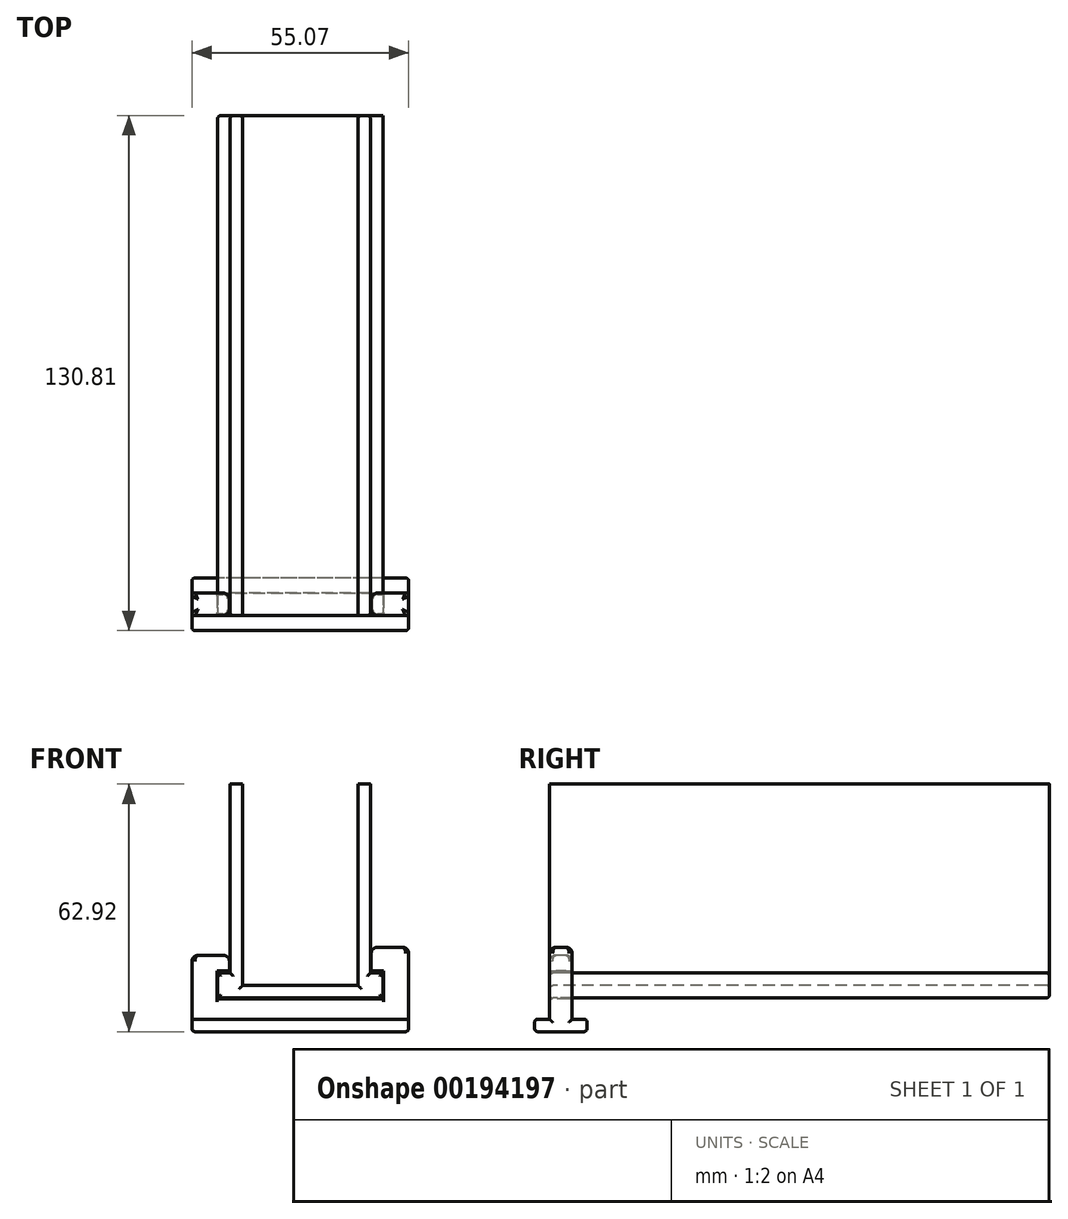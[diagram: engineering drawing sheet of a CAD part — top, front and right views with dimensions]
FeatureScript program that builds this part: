
annotation { "Feature Type Name" : "Feature", "Feature Type Description" : "" }
export const myFeature = defineFeature(function(context is Context, id is Id, definition is map)
    precondition{}
    {
        {
            var Q0;
            Q0=qCreatedBy(makeId("Front.planeOp"),FACE);
            var sketch = newSketch(context, id + "F0", { "sketchPlane" : qUnion([Q0])});
            skLineSegment(sketch, "E0", {"start": v(0, 8.52) * mm, "end": v(0, 0) * mm, "construction": true});
            skLineSegment(sketch, "E1.0", {"start": v(13.51, -0.38) * mm, "end": v(13.51, 50.8) * mm});
            skLineSegment(sketch, "E1.5", {"start": v(-15.8, 50.8) * mm, "end": v(-15.8, -0.38) * mm});
            skLineSegment(sketch, "E1.8", {"start": v(13.51, -0.38) * mm, "end": v(-15.8, -0.38) * mm});
            skLineSegment(sketch, "E2", {"start": v(-15.8, 50.8) * mm, "end": v(-18.97, 50.8) * mm});
            skLineSegment(sketch, "E3", {"start": v(-18.97, 50.8) * mm, "end": v(-18.97, 2.8) * mm});
            skLineSegment(sketch, "E4", {"start": v(-18.97, 2.8) * mm, "end": v(-22.15, 2.8) * mm});
            skLineSegment(sketch, "E5", {"start": v(-22.15, 2.8) * mm, "end": v(-22.15, -3.56) * mm});
            skLineSegment(sketch, "E6", {"start": v(-22.15, -3.56) * mm, "end": v(19.86, -3.56) * mm});
            skCircle(sketch, "E7", {"center": v(0, 5.02) * mm, "radius": 1.7 * mm, "construction": true});
            skLineSegment(sketch, "E8", {"start": v(13.51, 50.8) * mm, "end": v(16.69, 50.8) * mm});
            skLineSegment(sketch, "E9", {"start": v(16.69, 50.8) * mm, "end": v(16.69, 2.8) * mm});
            skLineSegment(sketch, "E10", {"start": v(16.69, 2.8) * mm, "end": v(19.86, 2.8) * mm});
            skLineSegment(sketch, "E11", {"start": v(19.86, 2.8) * mm, "end": v(19.86, -3.56) * mm});
            skLineSegment(sketch, "E12.0", {"start": v(16.87, 50.8) * mm, "end": v(16.87, 2.97) * mm});
            skLineSegment(sketch, "E12.1", {"start": v(16.87, 2.97) * mm, "end": v(20.04, 2.97) * mm});
            skLineSegment(sketch, "E12.2", {"start": v(20.04, 2.97) * mm, "end": v(20.04, -3.73) * mm});
            skLineSegment(sketch, "E12.3", {"start": v(-19.15, 50.8) * mm, "end": v(-19.15, 2.97) * mm});
            skLineSegment(sketch, "E12.4", {"start": v(-19.15, 2.97) * mm, "end": v(-22.33, 2.97) * mm});
            skLineSegment(sketch, "E12.5", {"start": v(-22.33, 2.97) * mm, "end": v(-22.33, -3.73) * mm});
            skLineSegment(sketch, "E12.6", {"start": v(-22.33, -3.73) * mm, "end": v(20.04, -3.73) * mm});
            skLineSegment(sketch, "E13.1", {"start": v(16.87, 9.32) * mm, "end": v(26.4, 9.32) * mm});
            skLineSegment(sketch, "E13.2", {"start": v(26.4, 9.32) * mm, "end": v(26.4, -12.12) * mm});
            skLineSegment(sketch, "E13.4", {"start": v(-19.15, 7.29) * mm, "end": v(-28.68, 7.29) * mm});
            skLineSegment(sketch, "E13.5", {"start": v(-28.68, 7.29) * mm, "end": v(-28.68, -12.12) * mm});
            skLineSegment(sketch, "E13.6", {"start": v(-28.68, -12.12) * mm, "end": v(26.4, -12.12) * mm});
            skSolve(sketch);
        }
        {
            var Q0;
            {var subQ1=sQuery(id+"F0.wireOp",EDGE,"E12.1");Q0=makeQuery(id+"F0.imprint","IMPRINT",FACE,{"disambiguationData":[TD([[makeQuery(id+"F0.imprint","IMPRINT",EDGE,{"derivedFrom":subQ1}),1.0]])]});}
            extrude(context, id + "F1", {"entities" : qUnion([Q0]), "oppositeDirection" : true, "depth" : 5.7 * mm});
        }
        {
            var Q0;
            Q0=makeQuery(id+"F1.opExtrude","CAP_EDGE",EDGE,{"disambiguationData":[OSD([sQuery(id+"F0.wireOp",EDGE,"E12.0")])],"isStart":true});
            var Q1;
            Q1=makeQuery(id+"F1.opExtrude","CAP_EDGE",EDGE,{"disambiguationData":[OSD([sQuery(id+"F0.wireOp",EDGE,"E12.0")])],"isStart":false});
            var Q2;
            Q2=makeQuery(id+"F1.opExtrude","CAP_EDGE",EDGE,{"disambiguationData":[OSD([sQuery(id+"F0.wireOp",EDGE,"E12.3")])],"isStart":true});
            var Q3;
            Q3=makeQuery(id+"F1.opExtrude","CAP_EDGE",EDGE,{"disambiguationData":[OSD([sQuery(id+"F0.wireOp",EDGE,"E13.4")])],"isStart":false});
            var Q4;
            Q4=makeQuery(id+"F1.opExtrude","CAP_EDGE",EDGE,{"disambiguationData":[OSD([sQuery(id+"F0.wireOp",EDGE,"E13.1")])],"isStart":false});
            var Q5;
            Q5=makeQuery(id+"F1.opExtrude","SWEPT_EDGE",EDGE,{"disambiguationData":[OSD([sQuery(id+"F0.wireOp",EDGE,"E12.3"),sQuery(id+"F0.wireOp",EDGE,"E13.4")])]});
            var Q6;
            Q6=makeQuery(id+"F1.opExtrude","SWEPT_EDGE",EDGE,{"disambiguationData":[OSD([sQuery(id+"F0.wireOp",EDGE,"E12.0"),sQuery(id+"F0.wireOp",EDGE,"E13.1")])]});
            var Q7;
            Q7=makeQuery(id+"F1.opExtrude","SWEPT_EDGE",EDGE,{"disambiguationData":[OSD([sQuery(id+"F0.wireOp",EDGE,"E13.4"),sQuery(id+"F0.wireOp",EDGE,"E13.5")])]});
            var Q8;
            Q8=makeQuery(id+"F1.opExtrude","SWEPT_EDGE",EDGE,{"disambiguationData":[OSD([sQuery(id+"F0.wireOp",EDGE,"E13.1"),sQuery(id+"F0.wireOp",EDGE,"E13.2")])]});
            var Q9;
            Q9=makeQuery(id+"F1.opExtrude","CAP_EDGE",EDGE,{"disambiguationData":[OSD([sQuery(id+"F0.wireOp",EDGE,"E13.1")])],"isStart":true});
            var Q10;
            Q10=makeQuery(id+"F1.opExtrude","CAP_EDGE",EDGE,{"disambiguationData":[OSD([sQuery(id+"F0.wireOp",EDGE,"E13.4")])],"isStart":true});
            var Q11;
            Q11=makeQuery(id+"F1.opExtrude","CAP_EDGE",EDGE,{"disambiguationData":[OSD([sQuery(id+"F0.wireOp",EDGE,"E12.3")])],"isStart":false});
            fillet(context, id + "F2", {"entities" : qUnion([Q0, Q1, Q2, Q3, Q4, Q5, Q6, Q7, Q8, Q9, Q10, Q11]), "radius" : 1.57 * mm, "tangentPropagation" : true, "allowEdgeOverflow" : false});
        }
        {
            var Q0;
            Q0=makeQuery(id+"F1.opExtrude","SWEPT_EDGE",EDGE,{"disambiguationData":[OSD([sQuery(id+"F0.wireOp",EDGE,"E12.0"),sQuery(id+"F0.wireOp",EDGE,"E12.1")])]});
            var Q1;
            Q1=makeQuery(id+"F1.opExtrude","SWEPT_EDGE",EDGE,{"disambiguationData":[OSD([sQuery(id+"F0.wireOp",EDGE,"E12.3"),sQuery(id+"F0.wireOp",EDGE,"E12.4")])]});
            chamfer(context, id + "F3", {"entities" : qUnion([Q0, Q1]), "width" : 0.38 * mm, "tangentPropagation" : true});
        }
        {
            var Q0;
            Q0=qCreatedBy(makeId("Right.planeOp"),FACE);
            var sketch = newSketch(context, id + "F4", { "sketchPlane" : qUnion([Q0])});
            skLineSegment(sketch, "E14.0", {"start": v(5.72, -12.12) * mm, "end": v(0, -12.12) * mm});
            skLineSegment(sketch, "E15.0", {"start": v(0, 7.75) * mm, "end": v(0, -12.12) * mm});
            skLineSegment(sketch, "E16.0", {"start": v(5.72, 7.75) * mm, "end": v(5.72, -12.12) * mm});
            skLineSegment(sketch, "E17", {"start": v(0, -8.94) * mm, "end": v(-3.81, -8.94) * mm});
            skLineSegment(sketch, "E18", {"start": v(-3.81, -8.94) * mm, "end": v(-3.81, -12.12) * mm});
            skLineSegment(sketch, "E19", {"start": v(-3.81, -12.12) * mm, "end": v(0, -12.12) * mm});
            skLineSegment(sketch, "E20", {"start": v(5.72, -8.94) * mm, "end": v(9.53, -8.94) * mm});
            skLineSegment(sketch, "E21", {"start": v(9.53, -8.94) * mm, "end": v(9.53, -12.12) * mm});
            skLineSegment(sketch, "E22", {"start": v(9.53, -12.12) * mm, "end": v(5.72, -12.12) * mm});
            skSolve(sketch);
        }
        {
            var Q0;
            {var subQ2=sQuery(id+"F4.wireOp",EDGE,"E17");Q0=makeQuery(id+"F4.imprint","IMPRINT",FACE,{"disambiguationData":[TD([[makeQuery(id+"F4.imprint","IMPRINT",EDGE,{"derivedFrom":subQ2}),1.0]])]});}
            var Q1;
            {var subQ2=sQuery(id+"F4.wireOp",EDGE,"E20");Q1=makeQuery(id+"F4.imprint","IMPRINT",FACE,{"disambiguationData":[TD([[makeQuery(id+"F4.imprint","IMPRINT",EDGE,{"derivedFrom":subQ2}),-1.0]])]});}
            extrude(context, id + "F5", {"entities" : qUnion([Q0, Q1]), "operationType" : NewBodyOperationType.ADD, "depth" : 26.4 * mm, "hasSecondDirection" : true, "secondDirectionOppositeDirection" : true, "secondDirectionDepth" : 28.68 * mm});
        }
        {
            var Q0;
            Q0=makeQuery(id+"F5.opExtrude","SWEPT_EDGE",EDGE,{"disambiguationData":[OSD([sQuery(id+"F4.wireOp",EDGE,"E17"),sQuery(id+"F4.wireOp",EDGE,"E18")])]});
            var Q1;
            Q1=makeQuery(id+"F5.opExtrude","SWEPT_EDGE",EDGE,{"disambiguationData":[OSD([sQuery(id+"F4.wireOp",EDGE,"E18"),sQuery(id+"F4.wireOp",EDGE,"E19")])]});
            var Q2;
            Q2=makeQuery(id+"F5.opExtrude","SWEPT_EDGE",EDGE,{"disambiguationData":[OSD([sQuery(id+"F4.wireOp",EDGE,"E20"),sQuery(id+"F4.wireOp",EDGE,"E21")])]});
            var Q3;
            Q3=makeQuery(id+"F5.opExtrude","SWEPT_EDGE",EDGE,{"disambiguationData":[OSD([sQuery(id+"F4.wireOp",EDGE,"E21"),sQuery(id+"F4.wireOp",EDGE,"E22")])]});
            var Q4;
            Q4=makeQuery(id+"F1.opExtrude","CAP_EDGE",EDGE,{"disambiguationData":[OSD([sQuery(id+"F0.wireOp",EDGE,"E13.2")])],"isStart":false});
            var Q5;
            Q5=makeQuery(id+"F1.opExtrude","CAP_EDGE",EDGE,{"disambiguationData":[OSD([sQuery(id+"F0.wireOp",EDGE,"E13.2")])],"isStart":true});
            var Q6;
            Q6=makeQuery(id+"F1.opExtrude","CAP_EDGE",EDGE,{"disambiguationData":[OSD([sQuery(id+"F0.wireOp",EDGE,"E13.5")])],"isStart":true});
            var Q7;
            Q7=makeQuery(id+"F1.opExtrude","CAP_EDGE",EDGE,{"disambiguationData":[OSD([sQuery(id+"F0.wireOp",EDGE,"E13.5")])],"isStart":false});
            var Q8;
            Q8=makeQuery(id+"F5.opExtrude","CAP_EDGE",EDGE,{"disambiguationData":[OSD([sQuery(id+"F4.wireOp",EDGE,"E20")])],"isStart":true});
            var Q9;
            Q9=makeQuery(id+"F5.opExtrude","CAP_EDGE",EDGE,{"disambiguationData":[OSD([sQuery(id+"F4.wireOp",EDGE,"E17")])],"isStart":true});
            var Q10;
            Q10=makeQuery(id+"F5.opExtrude","CAP_EDGE",EDGE,{"disambiguationData":[OSD([sQuery(id+"F4.wireOp",EDGE,"E17")])],"isStart":false});
            var Q11;
            Q11=makeQuery(id+"F5.opExtrude","CAP_EDGE",EDGE,{"disambiguationData":[OSD([sQuery(id+"F4.wireOp",EDGE,"E20")])],"isStart":false});
            var Q12;
            Q12=makeQuery(id+"F1.opExtrude","CAP_EDGE",EDGE,{"disambiguationData":[OSD([sQuery(id+"F0.wireOp",EDGE,"E12.6")])],"isStart":true});
            var Q13;
            Q13=makeQuery(id+"F1.opExtrude","CAP_EDGE",EDGE,{"disambiguationData":[OSD([sQuery(id+"F0.wireOp",EDGE,"E12.6")])],"isStart":false});
            var Q14;
            Q14=makeQuery(id+"F5.opExtrude","CAP_EDGE",EDGE,{"disambiguationData":[OSD([sQuery(id+"F4.wireOp",EDGE,"E21")])],"isStart":true});
            var Q15;
            Q15=makeQuery(id+"F5.opExtrude","CAP_EDGE",EDGE,{"disambiguationData":[OSD([sQuery(id+"F4.wireOp",EDGE,"E18")])],"isStart":true});
            var Q16;
            Q16=makeQuery(id+"F5.opExtrude","CAP_EDGE",EDGE,{"disambiguationData":[OSD([sQuery(id+"F4.wireOp",EDGE,"E18")])],"isStart":false});
            var Q17;
            Q17=makeQuery(id+"F5.opExtrude","CAP_EDGE",EDGE,{"disambiguationData":[OSD([sQuery(id+"F4.wireOp",EDGE,"E21")])],"isStart":false});
            var Q18;
            Q18=makeQuery(id+"F5.boolean.opBoolean","MERGE",EDGE,{"derivedFrom":[makeQuery(id+"F1.opExtrude","SWEPT_EDGE",EDGE,{"disambiguationData":[OSD([sQuery(id+"F0.wireOp",EDGE,"E13.2"),sQuery(id+"F0.wireOp",EDGE,"E13.6")])]}),makeQuery(id+"F5.opExtrude","CAP_EDGE",EDGE,{"disambiguationData":[OSD([sQuery(id+"F4.wireOp",EDGE,"E19")])],"isStart":false}),makeQuery(id+"F5.opExtrude","CAP_EDGE",EDGE,{"disambiguationData":[OSD([sQuery(id+"F4.wireOp",EDGE,"E22")])],"isStart":false})]});
            var Q19;
            Q19=makeQuery(id+"F5.boolean.opBoolean","MERGE",EDGE,{"derivedFrom":[makeQuery(id+"F1.opExtrude","SWEPT_EDGE",EDGE,{"disambiguationData":[OSD([sQuery(id+"F0.wireOp",EDGE,"E13.5"),sQuery(id+"F0.wireOp",EDGE,"E13.6")])]}),makeQuery(id+"F5.opExtrude","CAP_EDGE",EDGE,{"disambiguationData":[OSD([sQuery(id+"F4.wireOp",EDGE,"E19")])],"isStart":true}),makeQuery(id+"F5.opExtrude","CAP_EDGE",EDGE,{"disambiguationData":[OSD([sQuery(id+"F4.wireOp",EDGE,"E22")])],"isStart":true})]});
            fillet(context, id + "F6", {"entities" : qUnion([Q0, Q1, Q2, Q3, Q4, Q5, Q6, Q7, Q8, Q9, Q10, Q11, Q12, Q13, Q14, Q15, Q16, Q17, Q18, Q19]), "radius" : 0.79 * mm, "tangentPropagation" : true, "allowEdgeOverflow" : false});
        }
        {
            var Q0;
            Q0=makeQuery(id+"F0.imprint","IMPRINT",FACE,{"disambiguationData":[TD([[makeQuery(id+"F0.imprint","IMPRINT",EDGE,{"derivedFrom":sQuery(id+"F0.wireOp",EDGE,"E1.0")}),-1.0]])]});
            extrude(context, id + "F7", {"entities" : qUnion([Q0]), "oppositeDirection" : true, "depth" : 127 * mm});
        }
        {
            var Q0;
            Q0=makeQuery(id+"F9.boolean.opBoolean","INTERSECT",EDGE,{"derivedFrom":[makeQuery(id+"F7.opExtrude","SWEPT_FACE",FACE,{"disambiguationData":[OSD([sQuery(id+"F0.wireOp",EDGE,"E3")])]}),makeQuery(id+"F9.opExtrude","SWEPT_FACE",FACE,{"disambiguationData":[OSD([sQuery(id+"FkgncSVRvIpgr8o_1.wireOp",EDGE,"zSHfNMzP-miez-my1W-6nEw-eT44UZ99gvPm")])]})]});
            var Q1;
            Q1=makeQuery(id+"F9.boolean.opBoolean","INTERSECT",EDGE,{"derivedFrom":[makeQuery(id+"F7.opExtrude","SWEPT_FACE",FACE,{"disambiguationData":[OSD([sQuery(id+"F0.wireOp",EDGE,"E1.5")])]}),makeQuery(id+"F9.opExtrude","SWEPT_FACE",FACE,{"disambiguationData":[OSD([sQuery(id+"FkgncSVRvIpgr8o_1.wireOp",EDGE,"zSHfNMzP-miez-my1W-6nEw-eT44UZ99gvPm")])]})]});
            var Q2;
            Q2=makeQuery(id+"F7.opExtrude","CAP_EDGE",EDGE,{"disambiguationData":[OSD([sQuery(id+"F0.wireOp",EDGE,"E1.5")])],"isStart":true});
            var Q3;
            Q3=makeQuery(id+"F7.opExtrude","CAP_EDGE",EDGE,{"disambiguationData":[OSD([sQuery(id+"F0.wireOp",EDGE,"E9")])],"isStart":true});
            var Q4;
            Q4=makeQuery(id+"F9.boolean.opBoolean","INTERSECT",EDGE,{"derivedFrom":[makeQuery(id+"F7.opExtrude","SWEPT_FACE",FACE,{"disambiguationData":[OSD([sQuery(id+"F0.wireOp",EDGE,"E9")])]}),makeQuery(id+"F9.opExtrude","SWEPT_FACE",FACE,{"disambiguationData":[OSD([sQuery(id+"FkgncSVRvIpgr8o_1.wireOp",EDGE,"zSHfNMzP-miez-my1W-6nEw-eT44UZ99gvPm")])]})]});
            var Q5;
            Q5=makeQuery(id+"F9.boolean.opBoolean","INTERSECT",EDGE,{"derivedFrom":[makeQuery(id+"F7.opExtrude","SWEPT_FACE",FACE,{"disambiguationData":[OSD([sQuery(id+"F0.wireOp",EDGE,"E1.0")])]}),makeQuery(id+"F9.opExtrude","SWEPT_FACE",FACE,{"disambiguationData":[OSD([sQuery(id+"FkgncSVRvIpgr8o_1.wireOp",EDGE,"zSHfNMzP-miez-my1W-6nEw-eT44UZ99gvPm")])]})]});
            var Q6;
            Q6=makeQuery(id+"F7.opExtrude","CAP_EDGE",EDGE,{"disambiguationData":[OSD([sQuery(id+"F0.wireOp",EDGE,"E1.8")])],"isStart":true});
            var Q7;
            Q7=makeQuery(id+"F7.opExtrude","CAP_EDGE",EDGE,{"disambiguationData":[OSD([sQuery(id+"F0.wireOp",EDGE,"E3")])],"isStart":true});
            var Q8;
            Q8=makeQuery(id+"F7.opExtrude","CAP_EDGE",EDGE,{"disambiguationData":[OSD([sQuery(id+"F0.wireOp",EDGE,"E1.0")])],"isStart":true});
            var Q9;
            Q9=makeQuery(id+"F7.opExtrude","CAP_EDGE",EDGE,{"disambiguationData":[OSD([sQuery(id+"F0.wireOp",EDGE,"E6")])],"isStart":true});
            var Q10;
            Q10=makeQuery(id+"F7.opExtrude","CAP_EDGE",EDGE,{"disambiguationData":[OSD([sQuery(id+"F0.wireOp",EDGE,"E10")])],"isStart":true});
            var Q11;
            Q11=makeQuery(id+"F7.opExtrude","CAP_EDGE",EDGE,{"disambiguationData":[OSD([sQuery(id+"F0.wireOp",EDGE,"E11")])],"isStart":true});
            var Q12;
            Q12=makeQuery(id+"F7.opExtrude","CAP_EDGE",EDGE,{"disambiguationData":[OSD([sQuery(id+"F0.wireOp",EDGE,"E4")])],"isStart":true});
            var Q13;
            Q13=makeQuery(id+"F7.opExtrude","CAP_EDGE",EDGE,{"disambiguationData":[OSD([sQuery(id+"F0.wireOp",EDGE,"E5")])],"isStart":true});
            var Q14;
            Q14=makeQuery(id+"F8.boolean.opBoolean","INTERSECT",EDGE,{"derivedFrom":[makeQuery(id+"F7.opExtrude","SWEPT_FACE",FACE,{"disambiguationData":[OSD([sQuery(id+"F0.wireOp",EDGE,"E1.5")])]}),makeQuery(id+"F8.opExtrude","SWEPT_FACE",FACE,{"disambiguationData":[OSD([sQuery(id+"Fb2vMvGs9BCBtCK_1.wireOp",EDGE,"JCwaT7HA-nb2K-ZSJl-F4ic-s2mm5Mdn0rMo")])]})]});
            var Q15;
            Q15=makeQuery(id+"F8.boolean.opBoolean","INTERSECT",EDGE,{"derivedFrom":[makeQuery(id+"F7.opExtrude","SWEPT_FACE",FACE,{"disambiguationData":[OSD([sQuery(id+"F0.wireOp",EDGE,"E1.5")])]}),makeQuery(id+"F8.opExtrude","SWEPT_FACE",FACE,{"disambiguationData":[OSD([sQuery(id+"Fb2vMvGs9BCBtCK_1.wireOp",EDGE,"NnNVMowN-uRfN-1ljK-sG6J-4kigYHrPbNCR")])]})]});
            var Q16;
            Q16=makeQuery(id+"F8.boolean.opBoolean","INTERSECT",EDGE,{"derivedFrom":[makeQuery(id+"F7.opExtrude","SWEPT_FACE",FACE,{"disambiguationData":[OSD([sQuery(id+"F0.wireOp",EDGE,"E1.0")])]}),makeQuery(id+"F8.opExtrude","SWEPT_FACE",FACE,{"disambiguationData":[OSD([sQuery(id+"Fb2vMvGs9BCBtCK_1.wireOp",EDGE,"JCwaT7HA-nb2K-ZSJl-F4ic-s2mm5Mdn0rMo")])]})]});
            var Q17;
            Q17=makeQuery(id+"F8.boolean.opBoolean","INTERSECT",EDGE,{"derivedFrom":[makeQuery(id+"F7.opExtrude","SWEPT_FACE",FACE,{"disambiguationData":[OSD([sQuery(id+"F0.wireOp",EDGE,"E1.0")])]}),makeQuery(id+"F8.opExtrude","SWEPT_FACE",FACE,{"disambiguationData":[OSD([sQuery(id+"Fb2vMvGs9BCBtCK_1.wireOp",EDGE,"NnNVMowN-uRfN-1ljK-sG6J-4kigYHrPbNCR")])]})]});
            var Q18;
            Q18=makeQuery(id+"F8.boolean.opBoolean","INTERSECT",EDGE,{"derivedFrom":[makeQuery(id+"F7.opExtrude","SWEPT_FACE",FACE,{"disambiguationData":[OSD([sQuery(id+"F0.wireOp",EDGE,"E1.0")])]}),makeQuery(id+"F8.opExtrude","SWEPT_FACE",FACE,{"disambiguationData":[OSD([sQuery(id+"Fb2vMvGs9BCBtCK_1.wireOp",EDGE,"cyouxJAX-TsAO-8wIh-7wvX-UbvCRropZ8Xa")])]})]});
            var Q19;
            Q19=makeQuery(id+"F8.boolean.opBoolean","INTERSECT",EDGE,{"derivedFrom":[makeQuery(id+"F7.opExtrude","SWEPT_FACE",FACE,{"disambiguationData":[OSD([sQuery(id+"F0.wireOp",EDGE,"E1.0")])]}),makeQuery(id+"F8.opExtrude","SWEPT_FACE",FACE,{"disambiguationData":[OSD([sQuery(id+"Fb2vMvGs9BCBtCK_1.wireOp",EDGE,"2TtT8fLo-Forj-rr74-UrEx-JgbymLgOWg3h")])]})]});
            var Q20;
            Q20=makeQuery(id+"F8.boolean.opBoolean","INTERSECT",EDGE,{"derivedFrom":[makeQuery(id+"F7.opExtrude","SWEPT_FACE",FACE,{"disambiguationData":[OSD([sQuery(id+"F0.wireOp",EDGE,"E1.5")])]}),makeQuery(id+"F8.opExtrude","SWEPT_FACE",FACE,{"disambiguationData":[OSD([sQuery(id+"Fb2vMvGs9BCBtCK_1.wireOp",EDGE,"cyouxJAX-TsAO-8wIh-7wvX-UbvCRropZ8Xa")])]})]});
            var Q21;
            Q21=makeQuery(id+"F8.boolean.opBoolean","INTERSECT",EDGE,{"derivedFrom":[makeQuery(id+"F7.opExtrude","SWEPT_FACE",FACE,{"disambiguationData":[OSD([sQuery(id+"F0.wireOp",EDGE,"E1.5")])]}),makeQuery(id+"F8.opExtrude","SWEPT_FACE",FACE,{"disambiguationData":[OSD([sQuery(id+"Fb2vMvGs9BCBtCK_1.wireOp",EDGE,"2TtT8fLo-Forj-rr74-UrEx-JgbymLgOWg3h")])]})]});
            var Q22;
            Q22=makeQuery(id+"F7.opExtrude","CAP_EDGE",EDGE,{"disambiguationData":[OSD([sQuery(id+"F0.wireOp",EDGE,"E9")])],"isStart":false});
            var Q23;
            Q23=makeQuery(id+"F7.opExtrude","CAP_EDGE",EDGE,{"disambiguationData":[OSD([sQuery(id+"F0.wireOp",EDGE,"E10")])],"isStart":false});
            var Q24;
            Q24=makeQuery(id+"F7.opExtrude","CAP_EDGE",EDGE,{"disambiguationData":[OSD([sQuery(id+"F0.wireOp",EDGE,"E6")])],"isStart":false});
            var Q25;
            Q25=makeQuery(id+"F7.opExtrude","CAP_EDGE",EDGE,{"disambiguationData":[OSD([sQuery(id+"F0.wireOp",EDGE,"E5")])],"isStart":false});
            var Q26;
            Q26=makeQuery(id+"F7.opExtrude","CAP_EDGE",EDGE,{"disambiguationData":[OSD([sQuery(id+"F0.wireOp",EDGE,"E4")])],"isStart":false});
            var Q27;
            Q27=makeQuery(id+"F7.opExtrude","CAP_EDGE",EDGE,{"disambiguationData":[OSD([sQuery(id+"F0.wireOp",EDGE,"E3")])],"isStart":false});
            var Q28;
            Q28=makeQuery(id+"F7.opExtrude","CAP_EDGE",EDGE,{"disambiguationData":[OSD([sQuery(id+"F0.wireOp",EDGE,"E1.5")])],"isStart":false});
            var Q29;
            Q29=makeQuery(id+"F9.boolean.opBoolean","INTERSECT",EDGE,{"disambiguationData":[OD(1.0)],"derivedFrom":[makeQuery(id+"F7.opExtrude","CAP_FACE",FACE,{"disambiguationData":[OSD([sQuery(id+"F0.wireOp",EDGE,"E1.0"),sQuery(id+"F0.wireOp",EDGE,"E1.5"),sQuery(id+"F0.wireOp",EDGE,"E1.8"),sQuery(id+"F0.wireOp",EDGE,"E2"),sQuery(id+"F0.wireOp",EDGE,"E3"),sQuery(id+"F0.wireOp",EDGE,"E4"),sQuery(id+"F0.wireOp",EDGE,"E5"),sQuery(id+"F0.wireOp",EDGE,"E6"),sQuery(id+"F0.wireOp",EDGE,"E8"),sQuery(id+"F0.wireOp",EDGE,"E9"),sQuery(id+"F0.wireOp",EDGE,"E10"),sQuery(id+"F0.wireOp",EDGE,"E11")])],"isStart":false}),makeQuery(id+"F9.opExtrude","SWEPT_FACE",FACE,{"disambiguationData":[OSD([sQuery(id+"FkgncSVRvIpgr8o_1.wireOp",EDGE,"zSHfNMzP-miez-my1W-6nEw-eT44UZ99gvPm")])]})]});
            var Q30;
            Q30=makeQuery(id+"F7.opExtrude","CAP_EDGE",EDGE,{"disambiguationData":[OSD([sQuery(id+"F0.wireOp",EDGE,"E1.8")])],"isStart":false});
            var Q31;
            {var subQ0=sQuery(id+"F0.wireOp",EDGE,"E1.0");var subQ2=sQuery(id+"FkgncSVRvIpgr8o_1.wireOp",EDGE,"zSHfNMzP-miez-my1W-6nEw-eT44UZ99gvPm");Q31=makeQuery(id+"F9.boolean.opBoolean","COPY",EDGE,{"disambiguationData":[TD([makeQuery(id+"F7.opExtrude","SWEPT_FACE",FACE,{"disambiguationData":[OSD([subQ0])]})])],"derivedFrom":makeQuery(id+"F9.opExtrude","SWEPT_EDGE",EDGE,{"disambiguationData":[OSD([subQ2,sQuery(id+"FkgncSVRvIpgr8o_1.wireOp",EDGE,"rKgiiHri-59Wj-NHme-NQhZ-ddvmJMidBjXU")])]})});}
            var Q32;
            {var subQ1=sQuery(id+"F0.wireOp",EDGE,"E1.5");var subQ2=sQuery(id+"FkgncSVRvIpgr8o_1.wireOp",EDGE,"zSHfNMzP-miez-my1W-6nEw-eT44UZ99gvPm");Q32=makeQuery(id+"F9.boolean.opBoolean","COPY",EDGE,{"disambiguationData":[TD([makeQuery(id+"F7.opExtrude","SWEPT_FACE",FACE,{"disambiguationData":[OSD([subQ1])]})])],"derivedFrom":makeQuery(id+"F9.opExtrude","SWEPT_EDGE",EDGE,{"disambiguationData":[OSD([subQ2,sQuery(id+"FkgncSVRvIpgr8o_1.wireOp",EDGE,"rKgiiHri-59Wj-NHme-NQhZ-ddvmJMidBjXU")])]})});}
            var Q33;
            Q33=makeQuery(id+"F9.boolean.opBoolean","INTERSECT",EDGE,{"disambiguationData":[OD(0.0)],"derivedFrom":[makeQuery(id+"F7.opExtrude","CAP_FACE",FACE,{"disambiguationData":[OSD([sQuery(id+"F0.wireOp",EDGE,"E1.0"),sQuery(id+"F0.wireOp",EDGE,"E1.5"),sQuery(id+"F0.wireOp",EDGE,"E1.8"),sQuery(id+"F0.wireOp",EDGE,"E2"),sQuery(id+"F0.wireOp",EDGE,"E3"),sQuery(id+"F0.wireOp",EDGE,"E4"),sQuery(id+"F0.wireOp",EDGE,"E5"),sQuery(id+"F0.wireOp",EDGE,"E6"),sQuery(id+"F0.wireOp",EDGE,"E8"),sQuery(id+"F0.wireOp",EDGE,"E9"),sQuery(id+"F0.wireOp",EDGE,"E10"),sQuery(id+"F0.wireOp",EDGE,"E11")])],"isStart":false}),makeQuery(id+"F9.opExtrude","SWEPT_FACE",FACE,{"disambiguationData":[OSD([sQuery(id+"FkgncSVRvIpgr8o_1.wireOp",EDGE,"zSHfNMzP-miez-my1W-6nEw-eT44UZ99gvPm")])]})]});
            var Q34;
            Q34=makeQuery(id+"F7.opExtrude","CAP_EDGE",EDGE,{"disambiguationData":[OSD([sQuery(id+"F0.wireOp",EDGE,"E1.0")])],"isStart":false});
            fillet(context, id + "F10", {"entities" : qUnion([Q0, Q1, Q2, Q3, Q4, Q5, Q6, Q7, Q8, Q9, Q10, Q11, Q12, Q13, Q14, Q15, Q16, Q17, Q18, Q19, Q20, Q21, Q22, Q23, Q24, Q25, Q26, Q27, Q28, Q29, Q30, Q31, Q32, Q33, Q34]), "radius" : 0.81 * mm, "tangentPropagation" : true, "allowEdgeOverflow" : false});
        }
    });
